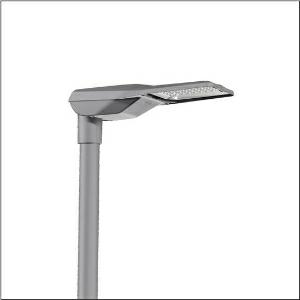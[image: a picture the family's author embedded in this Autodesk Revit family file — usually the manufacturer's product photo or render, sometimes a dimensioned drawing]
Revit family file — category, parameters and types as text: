
# Revit family: streetlight_sl_21_iq_mini___p0_8a_5xe2u31d08jb_69dd
name_source: partatom
category: Lighting Fixtures
units: mm (PartAtom-declared; Revit-internal decimal feet)

## family parameters
Cut with Voids When Loaded = No
Host = Face
Light Source = No
Part Type = Normal
Room Calculation Point = No
Round Connector Dimension = Use Diameter
Shared = No

## types (1)
- --- (1 x LED, 10920 lm, 71.6 W, 3000K)
    Apparent Load = 72 VA
    CIE Flux Codes = 36 69 97 100 100
    Color Rendering = 70
    Color Temperature = 3000K
    Default Elevation = 1800 mm
    Description = Streetlight SL 21 iQ mini, mast luminaire, primary light control with lens, of PMMA, primary optical cover: cover, of toughened safety glass, transparent, light distribution: P0.8a, light emission: direct distribution, primary light characteristic: asymmetric, installation type: post-top, side-entry, LED, High Power LED, rated luminous flux: 10.920lm, luminous efficacy: 153lm/W, light colour: 730, colour temperature: 3000K, control gear: iQ-Comfort, control: pre-setting: linear dimming characteristic, Auto-Match, Temp-Guard, Lumen-Switch, Night-Set, Smart-Wire, Light-Fading, Desk-Remote (wireless, voltage-free reading and setting of iQ features in the workshop via application-optimized NFC function/RFID function), optimised constant luminous flux control (CLO 2.0), mains connection: 220..240V, AC, 50/60Hz, start of lifetime: 72W, end of service life: 75W, reduction: 33W, luminaire housing, of diecast aluminium, powder-coated, SITECO metallic grey (DB 702S), corrosivity category C5 high according to DIN EN ISO 12944, please order mast flange separately, inclination adjustable: 0°, 5°, 10°, 15°, sealing non-destructively replaceable, multi-level sealing system, length: 628mm, width: 235mm, height: 110mm, mast flange for spigot size: 42mm (side-entry): 5XC10008XM4, 60/48mm (side-entry/post-top): 5XC10108XM2, 76/60mm (side-entry/post-top): 5XC10108XM1, mounting height: 4..8m, protection rating (complete): IP66, insulation class (complete): insulation class II (safety insulation), certification: CE, ENEC, ENEC+, VDE, impact resistance: IK10, permissible operating ambient temperature for outdoor applications: -40..+50°C, standard-compliant lighting for roads and squares, packaging unit: 1 piece

Light Distribution: P0.8a
    Height = 110 mm
    Lamp = 1 x LED
    Lamp Light Flux = 10920 lm
    Lamp Power = 71.6 W
    Lamp count = 1
    Length = 625 mm
    Luminous efficacy = 153 lm/W
    Manufacturer = Siteco
    ModVariant = No
    Model = 5XE2U31D08JB
    Number of Poles = 1
    OnlyDefault = Yes
    Power Factor = 1
    Product Name = Streetlight SL 21 iQ mini | P0.8a
    Product group = mast luminaire | pylon top
    ProductGroupID = 6100
    Protection Class = Protection class II
    Protection Degree = IP 66
    RLX_Detail_Level = 1
    RLX_Emergency_Light_Flux = 0 lm
    RLX_Emergency_Type = 0
    RLX_Emergency_Type_DB = No
    RlxData = <blob elided: 92181 chars, md5=843441dd>
    Socket = socket
    Standby Power = 0 W
    System Light Flux = 10920 lm
    System Power = 72 W
    Type Comments = factory setting: luminous flux: 100 % | dim-lin: 254 | 746 mA
    Type Image = l_1003519.jpg
    URL = http://relux.com
    VarID = @adj_079375
    Voltage = 0 V
    Weight = 0.00 kg
    Width = 234 mm

## geometry (parser evidence)
native form markers: Blend x4, Sweep x9
no freeform markers — native parametric forms only
